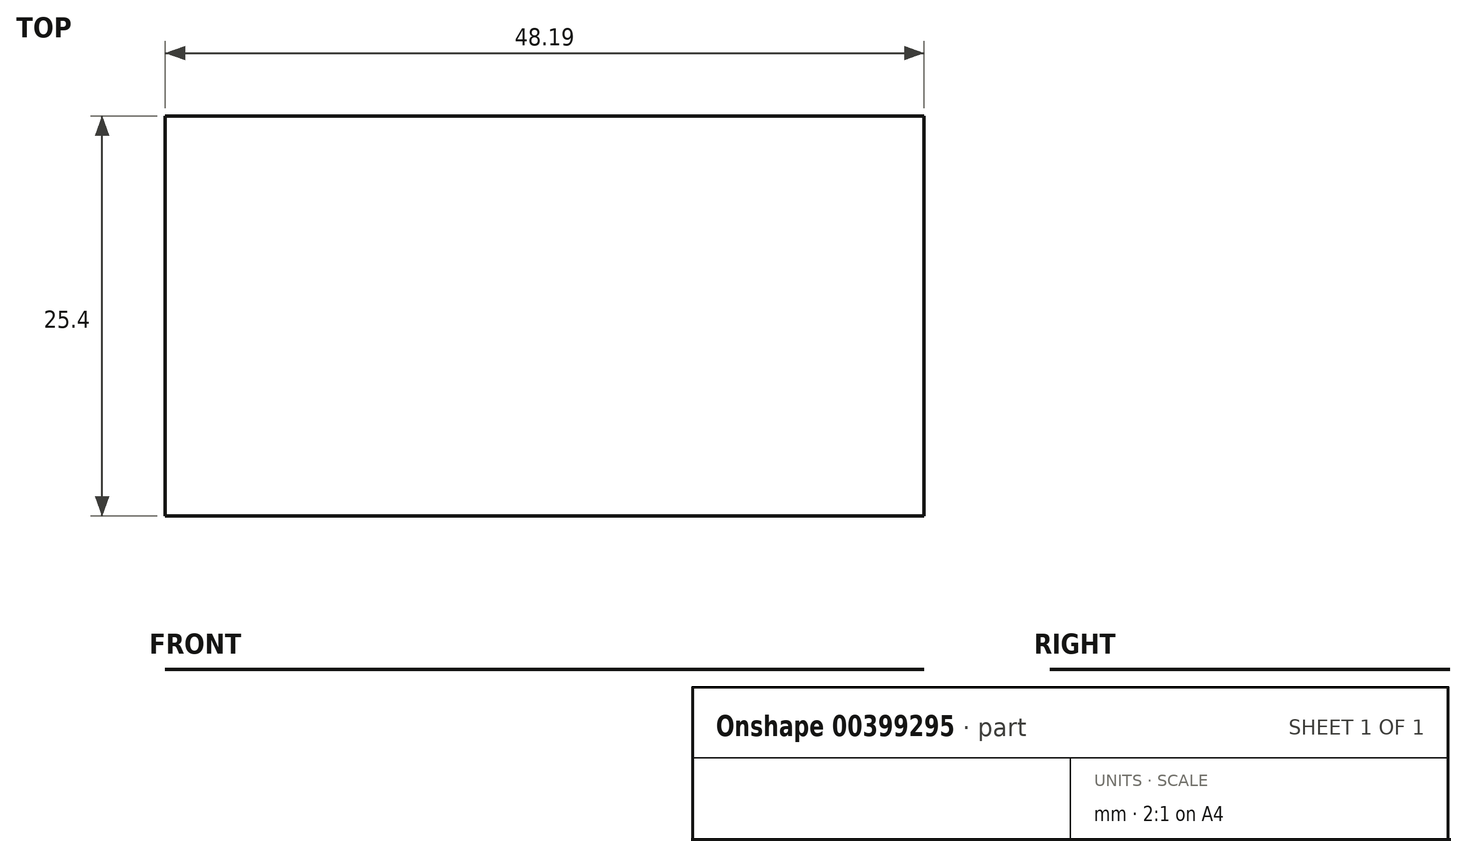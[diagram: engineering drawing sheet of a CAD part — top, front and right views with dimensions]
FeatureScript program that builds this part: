
annotation { "Feature Type Name" : "Feature", "Feature Type Description" : "" }
export const myFeature = defineFeature(function(context is Context, id is Id, definition is map)
    precondition{}
    {
        {
            var Q0;
            Q0=qCreatedBy(makeId("Front.planeOp"),FACE);
            var sketch = newSketch(context, id + "F0", { "sketchPlane" : qUnion([Q0])});
            skLineSegment(sketch, "E0.bottom", {"start": v(38.13, 36.73) * mm, "end": v(58.3, 36.73) * mm});
            skLineSegment(sketch, "E0.top", {"start": v(38.13, 13.54) * mm, "end": v(58.3, 13.54) * mm});
            skLineSegment(sketch, "E0.left", {"start": v(38.13, 36.73) * mm, "end": v(38.13, 13.54) * mm});
            skLineSegment(sketch, "E0.right", {"start": v(58.3, 36.73) * mm, "end": v(58.3, 13.54) * mm});
            skLineSegment(sketch, "E1.bottom", {"start": v(68.1, 0) * mm, "end": v(116.3, 0) * mm});
            skLineSegment(sketch, "E1.top", {"start": v(68.1, -12.35) * mm, "end": v(116.3, -12.35) * mm});
            skLineSegment(sketch, "E1.left", {"start": v(68.1, 0) * mm, "end": v(68.1, -12.35) * mm});
            skLineSegment(sketch, "E1.right", {"start": v(116.3, 0) * mm, "end": v(116.3, -12.35) * mm});
            skSolve(sketch);
        }
        {
            var Q0;
            Q0 = qSketchRegion(id + "F0", true);
            var Q1;
            Q1=sQuery(id+"F0.wireOp",EDGE,"E1.bottom");
            extrude(context, id + "F1", {"entities" : qUnion([Q0]), "bodyType" : ToolBodyType.SURFACE, "surfaceEntities" : qUnion([Q1]), "depth" : 25.4 * mm});
        }
    });
